# Revit family: ArandelaConcreto_ASC6W_ASC11W_PowerLume
name_source: partatom
category: Luminárias
units: mm (PartAtom-declared; Revit-internal decimal feet)

## family parameters
Compartilhado = Não
Corte com vazios quando carregada = Sim
Cota do conector redondo = Utilizar diâmetro
Fonte luminosa = Não
Hospedeiro = Face
Manter orientação da anotação = Não
Número OmniClass = 23.80.70.14.11.17
Ponto de cálculo do ambiente = Não
Tipo de parte = Normal
Título OmniClass = Wall or Ceiling Mounted External Lighting

## types (2) — shared parameters
Carga Aparente Luminária = 0 VA
Catálogo de produtos = https://www.powerlume.com.br
Comentários de voltagem = 110 ou 220Vac 50/60Hz com driver incorporado
Contato do fabricante = (54) 3066-6488
Data da atualização = 27/02/2025
Descrição = Arandela de sobrepor LED em concreto
Difusor = PMMA transparente anti UV
Elevação-padrão = 1219 mm
Fabricante = Power Lume
Fator de Potência Luminária = 1
Frame = Concreto, leve
IP = 65
IRC = 85
IfcExportAs = IfcLightFixtureType
Localização = Caxias do Sul - RS / Brasil
Lâmpada = Placa LED
Peso = 0
Profundidade = 81 mm  [stored 0.265748 ft]
Temperatura de cor = 3000K
URL = https://www.powerlume.com.br
URL do produto = https://www.powerlume.com.br
Versão = 1
Vida útil = 60000h
Voltagem Luminária = 0 V
Ângulo de abertura = Assimétrico

## per-type parameters (varying)
| type | Altura | Fluxo luminoso | Largura | Modelo de luminária | Potência | Tipo de imagem |
| ASC11W | 250 mm  [stored 0.82021 ft] | 931 lm | 350 mm  [stored 1.14829 ft] | ArandelaConcreto_ASC11W_Base_PowerLume : ASC11W | 11W | FOTO ASC11W.png |
| ASC6W | 150 mm | 465 lm | 250 mm  [stored 0.82021 ft] | ArandelaConcreto_ASC6W_Base_PowerLume : ASC6W | 6W | FOTO ASC6W.png |

note: column(s) folded — value = type name in every type: Modelo

note: [stored X ft] marks values corroborated as IEEE doubles in the binary element streams (Revit-internal decimal feet)
